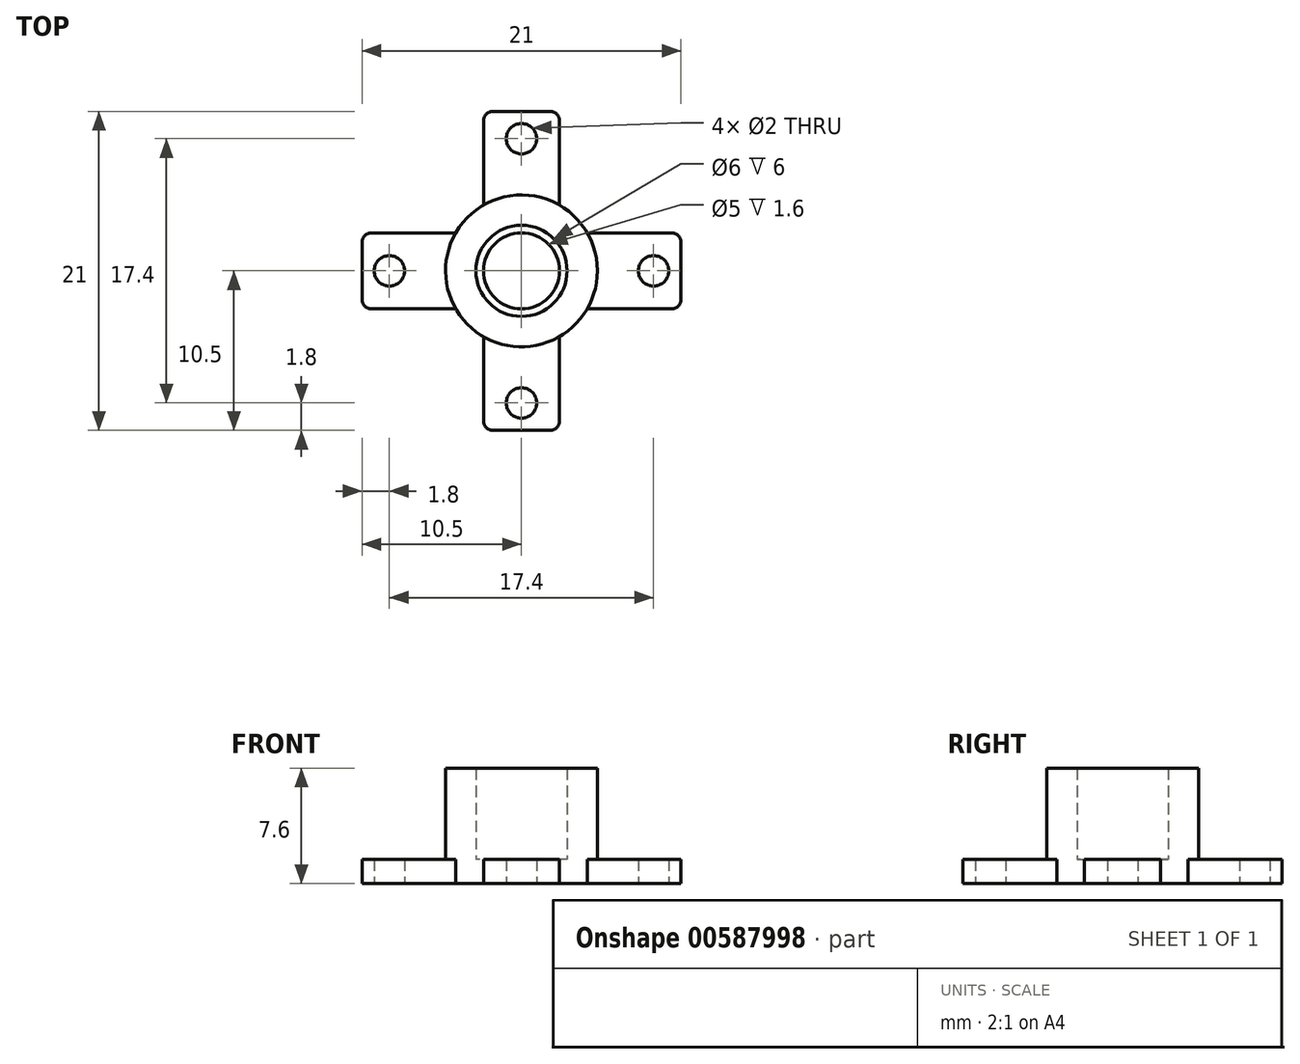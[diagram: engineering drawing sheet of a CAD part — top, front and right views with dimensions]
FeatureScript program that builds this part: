
annotation { "Feature Type Name" : "Feature", "Feature Type Description" : "" }
export const myFeature = defineFeature(function(context is Context, id is Id, definition is map)
    precondition{}
    {
        {
            var Q0;
            Q0=qCreatedBy(makeId("Top.planeOp"),FACE);
            var sketch = newSketch(context, id + "F0", { "sketchPlane" : qUnion([Q0])});
            skLineSegment(sketch, "E0.bottom", {"start": v(9.9, 2.5) * mm, "end": v(-9.9, 2.5) * mm});
            skLineSegment(sketch, "E0.top", {"start": v(9.9, -2.5) * mm, "end": v(-9.9, -2.5) * mm});
            skLineSegment(sketch, "E0.left", {"start": v(10.5, 1.9) * mm, "end": v(10.5, -1.9) * mm});
            skLineSegment(sketch, "E0.right", {"start": v(-10.5, 1.9) * mm, "end": v(-10.5, -1.9) * mm});
            skPoint(sketch, "E0.middle", {"position": v(0, 0) * mm});
            skLineSegment(sketch, "E1.bottom", {"start": v(1.9, 10.5) * mm, "end": v(-1.9, 10.5) * mm});
            skLineSegment(sketch, "E1.top", {"start": v(1.9, -10.5) * mm, "end": v(-1.9, -10.5) * mm});
            skLineSegment(sketch, "E1.left", {"start": v(2.5, 9.9) * mm, "end": v(2.5, -9.9) * mm});
            skLineSegment(sketch, "E1.right", {"start": v(-2.5, 9.9) * mm, "end": v(-2.5, -9.9) * mm});
            skCircle(sketch, "E2", {"center": v(8.7, 0) * mm, "radius": 1 * mm});
            skCircle(sketch, "E3.1.1", {"center": v(0, 8.7) * mm, "radius": 1 * mm});
            skCircle(sketch, "E3.2.1", {"center": v(-8.7, 0) * mm, "radius": 1 * mm});
            skCircle(sketch, "E3.3.1", {"center": v(0, -8.7) * mm, "radius": 1 * mm});
            skLineSegment(sketch, "E3.anchor1", {"start": v(0, 0) * mm, "end": v(8.7, 0) * mm, "construction": true});
            skLineSegment(sketch, "E3.anchor2", {"start": v(0, 0) * mm, "end": v(0, -8.7) * mm, "construction": true});
            skPoint(sketch, "E4.visualSharp", {"position": v(2.5, 10.5) * mm});
            skArc(sketch, "E4.filletArc", {"start": v(2.5, 9.9) * mm, "mid": v(2.32, 10.32) * mm, "end": v(1.9, 10.5) * mm});
            skPoint(sketch, "E5.visualSharp", {"position": v(-2.5, 10.5) * mm});
            skArc(sketch, "E5.filletArc", {"start": v(-1.9, 10.5) * mm, "mid": v(-2.32, 10.32) * mm, "end": v(-2.5, 9.9) * mm});
            skPoint(sketch, "E6.visualSharp", {"position": v(-2.5, -10.5) * mm});
            skArc(sketch, "E6.filletArc", {"start": v(-2.5, -9.9) * mm, "mid": v(-2.32, -10.32) * mm, "end": v(-1.9, -10.5) * mm});
            skPoint(sketch, "E7.visualSharp", {"position": v(2.5, -10.5) * mm});
            skArc(sketch, "E7.filletArc", {"start": v(1.9, -10.5) * mm, "mid": v(2.32, -10.32) * mm, "end": v(2.5, -9.9) * mm});
            skPoint(sketch, "E8.visualSharp", {"position": v(10.5, -2.5) * mm});
            skArc(sketch, "E8.filletArc", {"start": v(9.9, -2.5) * mm, "mid": v(10.32, -2.32) * mm, "end": v(10.5, -1.9) * mm});
            skPoint(sketch, "E9.visualSharp", {"position": v(10.5, 2.5) * mm});
            skArc(sketch, "E9.filletArc", {"start": v(10.5, 1.9) * mm, "mid": v(10.32, 2.32) * mm, "end": v(9.9, 2.5) * mm});
            skPoint(sketch, "E10.visualSharp", {"position": v(-10.5, 2.5) * mm});
            skArc(sketch, "E10.filletArc", {"start": v(-9.9, 2.5) * mm, "mid": v(-10.32, 2.32) * mm, "end": v(-10.5, 1.9) * mm});
            skPoint(sketch, "E11.visualSharp", {"position": v(-10.5, -2.5) * mm});
            skArc(sketch, "E11.filletArc", {"start": v(-10.5, -1.9) * mm, "mid": v(-10.32, -2.32) * mm, "end": v(-9.9, -2.5) * mm});
            skSolve(sketch);
        }
        {
            var Q0;
            Q0 = qSketchRegion(id + "F0", true);
            extrude(context, id + "F1", {"entities" : qUnion([Q0]), "depth" : 1.6 * mm, "offsetDistance" : 25 * mm});
        }
        {
            var Q0;
            Q0=makeQuery(id+"F1.opExtrude","CAP_FACE",FACE,{"disambiguationData":[OSD([sQuery(id+"F0.wireOp",EDGE,"E0.bottom"),sQuery(id+"F0.wireOp",EDGE,"E0.top"),sQuery(id+"F0.wireOp",EDGE,"E0.left"),sQuery(id+"F0.wireOp",EDGE,"E0.right"),sQuery(id+"F0.wireOp",EDGE,"E1.bottom"),sQuery(id+"F0.wireOp",EDGE,"E1.top"),sQuery(id+"F0.wireOp",EDGE,"E1.left"),sQuery(id+"F0.wireOp",EDGE,"E1.right"),sQuery(id+"F0.wireOp",EDGE,"E2"),sQuery(id+"F0.wireOp",EDGE,"E3.1.1"),sQuery(id+"F0.wireOp",EDGE,"E3.2.1"),sQuery(id+"F0.wireOp",EDGE,"E3.3.1"),sQuery(id+"F0.wireOp",EDGE,"E4.filletArc"),sQuery(id+"F0.wireOp",EDGE,"E5.filletArc"),sQuery(id+"F0.wireOp",EDGE,"E6.filletArc"),sQuery(id+"F0.wireOp",EDGE,"E7.filletArc"),sQuery(id+"F0.wireOp",EDGE,"E8.filletArc"),sQuery(id+"F0.wireOp",EDGE,"E9.filletArc"),sQuery(id+"F0.wireOp",EDGE,"E10.filletArc"),sQuery(id+"F0.wireOp",EDGE,"E11.filletArc")])],"isStart":false});
            var sketch = newSketch(context, id + "F2", { "sketchPlane" : qUnion([Q0])});
            skCircle(sketch, "E12", {"center": v(0, 0) * mm, "radius": 5 * mm});
            skCircle(sketch, "E13", {"center": v(0, 0) * mm, "radius": 3 * mm});
            skSolve(sketch);
        }
        {
            var Q0;
            Q0=makeQuery(id+"F2.imprint","IMPRINT",FACE,{"disambiguationData":[TD([[makeQuery(id+"F2.imprint","IMPRINT",EDGE,{"derivedFrom":sQuery(id+"F2.wireOp",EDGE,"E13")}),-1.0]])]});
            var Q1;
            {var subQ0=sQuery(id+"F2.wireOp",EDGE,"E12");var subQ1=sQuery(id+"F0.wireOp",EDGE,"E0.top");var subQ4=makeQuery(id+"F1.opExtrude","CAP_EDGE",EDGE,{"disambiguationData":[OSD([subQ1]),TDD([makeQuery(id+"F0.imprint","IMPRINT",EDGE,{"disambiguationData":[TD([[makeQuery(id+"F0.imprint","INTERSECT",VERTEX,{"derivedFrom":[subQ1,sQuery(id+"F0.wireOp",EDGE,"E11.filletArc")]}),1.0]])],"derivedFrom":subQ1})])],"isStart":false});var subQ5=makeQuery(id+"F2.imprint","INTERSECT",VERTEX,{"derivedFrom":[subQ4,subQ0]});Q1=makeQuery(id+"F2.imprint","IMPRINT",FACE,{"disambiguationData":[TD([[makeQuery(id+"F2.imprint","IMPRINT",EDGE,{"disambiguationData":[TD([[subQ5,-1.0]])],"derivedFrom":subQ0}),1.0]])]});}
            var Q2;
            {var subQ0=sQuery(id+"F2.wireOp",EDGE,"E12");var subQ1=sQuery(id+"F0.wireOp",EDGE,"E1.left");var subQ4=makeQuery(id+"F1.opExtrude","CAP_EDGE",EDGE,{"disambiguationData":[OSD([subQ1]),TDD([makeQuery(id+"F0.imprint","IMPRINT",EDGE,{"disambiguationData":[TD([[makeQuery(id+"F0.imprint","INTERSECT",VERTEX,{"derivedFrom":[subQ1,sQuery(id+"F0.wireOp",EDGE,"E7.filletArc")]}),1.0]])],"derivedFrom":subQ1})])],"isStart":false});var subQ5=makeQuery(id+"F2.imprint","INTERSECT",VERTEX,{"derivedFrom":[subQ4,subQ0]});Q2=makeQuery(id+"F2.imprint","IMPRINT",FACE,{"disambiguationData":[TD([[makeQuery(id+"F2.imprint","IMPRINT",EDGE,{"disambiguationData":[TD([[subQ5,-1.0]])],"derivedFrom":subQ0}),1.0]])]});}
            var Q3;
            {var subQ0=sQuery(id+"F2.wireOp",EDGE,"E12");var subQ1=sQuery(id+"F0.wireOp",EDGE,"E1.left");var subQ4=makeQuery(id+"F1.opExtrude","CAP_EDGE",EDGE,{"disambiguationData":[OSD([subQ1]),TDD([makeQuery(id+"F0.imprint","IMPRINT",EDGE,{"disambiguationData":[TD([[makeQuery(id+"F0.imprint","INTERSECT",VERTEX,{"derivedFrom":[subQ1,sQuery(id+"F0.wireOp",EDGE,"E4.filletArc")]}),-1.0]])],"derivedFrom":subQ1})])],"isStart":false});var subQ5=makeQuery(id+"F2.imprint","INTERSECT",VERTEX,{"derivedFrom":[subQ4,subQ0]});Q3=makeQuery(id+"F2.imprint","IMPRINT",FACE,{"disambiguationData":[TD([[makeQuery(id+"F2.imprint","IMPRINT",EDGE,{"disambiguationData":[TD([[subQ5,1.0]])],"derivedFrom":subQ0}),1.0]])]});}
            var Q4;
            {var subQ0=sQuery(id+"F2.wireOp",EDGE,"E12");var subQ1=sQuery(id+"F0.wireOp",EDGE,"E1.right");var subQ4=makeQuery(id+"F1.opExtrude","CAP_EDGE",EDGE,{"disambiguationData":[OSD([subQ1]),TDD([makeQuery(id+"F0.imprint","IMPRINT",EDGE,{"disambiguationData":[TD([[makeQuery(id+"F0.imprint","INTERSECT",VERTEX,{"derivedFrom":[subQ1,sQuery(id+"F0.wireOp",EDGE,"E5.filletArc")]}),-1.0]])],"derivedFrom":subQ1})])],"isStart":false});var subQ5=makeQuery(id+"F2.imprint","INTERSECT",VERTEX,{"derivedFrom":[subQ4,subQ0]});Q4=makeQuery(id+"F2.imprint","IMPRINT",FACE,{"disambiguationData":[TD([[makeQuery(id+"F2.imprint","IMPRINT",EDGE,{"disambiguationData":[TD([[subQ5,-1.0]])],"derivedFrom":subQ0}),1.0]])]});}
            extrude(context, id + "F3", {"entities" : qUnion([Q0, Q1, Q2, Q3, Q4]), "operationType" : NewBodyOperationType.ADD, "depth" : 6 * mm, "offsetDistance" : 25 * mm});
        }
        {
            var Q0;
            {var subQ0=sQuery(id+"F0.wireOp",EDGE,"E10.filletArc");var subQ3=sQuery(id+"F0.wireOp",EDGE,"E0.bottom");var subQ5=sQuery(id+"F2.wireOp",EDGE,"E12");Q0=makeQuery(id+"F3.boolean.opBoolean","SPLIT",FACE,{"disambiguationData":[TD([makeQuery(id+"F1.opExtrude","SWEPT_FACE",FACE,{"disambiguationData":[OSD([subQ3]),TDD([makeQuery(id+"F0.imprint","IMPRINT",EDGE,{"disambiguationData":[TD([[makeQuery(id+"F0.imprint","INTERSECT",VERTEX,{"derivedFrom":[subQ3,subQ0]}),1.0]])],"derivedFrom":subQ3})])]})])],"derivedFrom":makeQuery(id+"F3.opExtrude","CAP_FACE",FACE,{"disambiguationData":[OSD([subQ5,sQuery(id+"F2.wireOp",EDGE,"E13")])],"isStart":true})});}
            var Q1;
            {var subQ0=sQuery(id+"F0.wireOp",EDGE,"E9.filletArc");var subQ1=sQuery(id+"F0.wireOp",EDGE,"E0.bottom");var subQ5=sQuery(id+"F2.wireOp",EDGE,"E12");Q1=makeQuery(id+"F3.boolean.opBoolean","SPLIT",FACE,{"disambiguationData":[TD([makeQuery(id+"F1.opExtrude","SWEPT_FACE",FACE,{"disambiguationData":[OSD([subQ1]),TDD([makeQuery(id+"F0.imprint","IMPRINT",EDGE,{"disambiguationData":[TD([[makeQuery(id+"F0.imprint","INTERSECT",VERTEX,{"derivedFrom":[subQ1,subQ0]}),-1.0]])],"derivedFrom":subQ1})])]})])],"derivedFrom":makeQuery(id+"F3.opExtrude","CAP_FACE",FACE,{"disambiguationData":[OSD([subQ5,sQuery(id+"F2.wireOp",EDGE,"E13")])],"isStart":true})});}
            var Q2;
            {var subQ0=sQuery(id+"F0.wireOp",EDGE,"E11.filletArc");var subQ3=sQuery(id+"F0.wireOp",EDGE,"E0.top");var subQ5=sQuery(id+"F2.wireOp",EDGE,"E12");Q2=makeQuery(id+"F3.boolean.opBoolean","SPLIT",FACE,{"disambiguationData":[TD([makeQuery(id+"F1.opExtrude","SWEPT_FACE",FACE,{"disambiguationData":[OSD([subQ3]),TDD([makeQuery(id+"F0.imprint","IMPRINT",EDGE,{"disambiguationData":[TD([[makeQuery(id+"F0.imprint","INTERSECT",VERTEX,{"derivedFrom":[subQ3,subQ0]}),1.0]])],"derivedFrom":subQ3})])]})])],"derivedFrom":makeQuery(id+"F3.opExtrude","CAP_FACE",FACE,{"disambiguationData":[OSD([subQ5,sQuery(id+"F2.wireOp",EDGE,"E13")])],"isStart":true})});}
            var Q3;
            {var subQ0=sQuery(id+"F0.wireOp",EDGE,"E8.filletArc");var subQ3=sQuery(id+"F0.wireOp",EDGE,"E0.top");var subQ5=sQuery(id+"F2.wireOp",EDGE,"E12");Q3=makeQuery(id+"F3.boolean.opBoolean","SPLIT",FACE,{"disambiguationData":[TD([makeQuery(id+"F1.opExtrude","SWEPT_FACE",FACE,{"disambiguationData":[OSD([subQ3]),TDD([makeQuery(id+"F0.imprint","IMPRINT",EDGE,{"disambiguationData":[TD([[makeQuery(id+"F0.imprint","INTERSECT",VERTEX,{"derivedFrom":[subQ3,subQ0]}),-1.0]])],"derivedFrom":subQ3})])]})])],"derivedFrom":makeQuery(id+"F3.opExtrude","CAP_FACE",FACE,{"disambiguationData":[OSD([subQ5,sQuery(id+"F2.wireOp",EDGE,"E13")])],"isStart":true})});}
            var Q4;
            Q4=makeQuery(id+"F1.opExtrude","CAP_FACE",FACE,{"disambiguationData":[OSD([sQuery(id+"F0.wireOp",EDGE,"E0.bottom"),sQuery(id+"F0.wireOp",EDGE,"E0.top"),sQuery(id+"F0.wireOp",EDGE,"E0.left"),sQuery(id+"F0.wireOp",EDGE,"E0.right"),sQuery(id+"F0.wireOp",EDGE,"E1.bottom"),sQuery(id+"F0.wireOp",EDGE,"E1.top"),sQuery(id+"F0.wireOp",EDGE,"E1.left"),sQuery(id+"F0.wireOp",EDGE,"E1.right"),sQuery(id+"F0.wireOp",EDGE,"E2"),sQuery(id+"F0.wireOp",EDGE,"E3.1.1"),sQuery(id+"F0.wireOp",EDGE,"E3.2.1"),sQuery(id+"F0.wireOp",EDGE,"E3.3.1"),sQuery(id+"F0.wireOp",EDGE,"E4.filletArc"),sQuery(id+"F0.wireOp",EDGE,"E5.filletArc"),sQuery(id+"F0.wireOp",EDGE,"E6.filletArc"),sQuery(id+"F0.wireOp",EDGE,"E7.filletArc"),sQuery(id+"F0.wireOp",EDGE,"E8.filletArc"),sQuery(id+"F0.wireOp",EDGE,"E9.filletArc"),sQuery(id+"F0.wireOp",EDGE,"E10.filletArc"),sQuery(id+"F0.wireOp",EDGE,"E11.filletArc")])],"isStart":true});
            extrude(context, id + "F4", {"entities" : qUnion([Q0, Q1, Q2, Q3]), "operationType" : NewBodyOperationType.ADD, "endBound" : BoundingType.UP_TO_SURFACE, "depth" : 25 * mm, "endBoundEntityFace" : qUnion([Q4]), "offsetDistance" : 25 * mm});
        }
        {
            var Q0;
            Q0=makeQuery(id+"F3.boolean.opBoolean","SPLIT",FACE,{"disambiguationData":[TD([makeQuery(id+"F3.opExtrude","SWEPT_FACE",FACE,{"disambiguationData":[OSD([sQuery(id+"F2.wireOp",EDGE,"E13")])]})])],"derivedFrom":makeQuery(id+"F1.opExtrude","CAP_FACE",FACE,{"disambiguationData":[OSD([sQuery(id+"F0.wireOp",EDGE,"E0.bottom"),sQuery(id+"F0.wireOp",EDGE,"E0.top"),sQuery(id+"F0.wireOp",EDGE,"E0.left"),sQuery(id+"F0.wireOp",EDGE,"E0.right"),sQuery(id+"F0.wireOp",EDGE,"E1.bottom"),sQuery(id+"F0.wireOp",EDGE,"E1.top"),sQuery(id+"F0.wireOp",EDGE,"E1.left"),sQuery(id+"F0.wireOp",EDGE,"E1.right"),sQuery(id+"F0.wireOp",EDGE,"E2"),sQuery(id+"F0.wireOp",EDGE,"E3.1.1"),sQuery(id+"F0.wireOp",EDGE,"E3.2.1"),sQuery(id+"F0.wireOp",EDGE,"E3.3.1"),sQuery(id+"F0.wireOp",EDGE,"E4.filletArc"),sQuery(id+"F0.wireOp",EDGE,"E5.filletArc"),sQuery(id+"F0.wireOp",EDGE,"E6.filletArc"),sQuery(id+"F0.wireOp",EDGE,"E7.filletArc"),sQuery(id+"F0.wireOp",EDGE,"E8.filletArc"),sQuery(id+"F0.wireOp",EDGE,"E9.filletArc"),sQuery(id+"F0.wireOp",EDGE,"E10.filletArc"),sQuery(id+"F0.wireOp",EDGE,"E11.filletArc")])],"isStart":false})});
            var sketch = newSketch(context, id + "F5", { "sketchPlane" : qUnion([Q0])});
            skCircle(sketch, "E14", {"center": v(0, 0) * mm, "radius": 2.5 * mm});
            skSolve(sketch);
        }
        {
            var Q0;
            Q0=makeQuery(id+"F5.imprint","IMPRINT",FACE,{"disambiguationData":[TD([[makeQuery(id+"F5.imprint","IMPRINT",EDGE,{"derivedFrom":sQuery(id+"F5.wireOp",EDGE,"E14")}),1.0]])]});
            extrude(context, id + "F6", {"entities" : qUnion([Q0]), "operationType" : NewBodyOperationType.REMOVE, "endBound" : BoundingType.UP_TO_NEXT, "oppositeDirection" : true, "depth" : 25 * mm, "offsetDistance" : 25 * mm});
        }
    });
